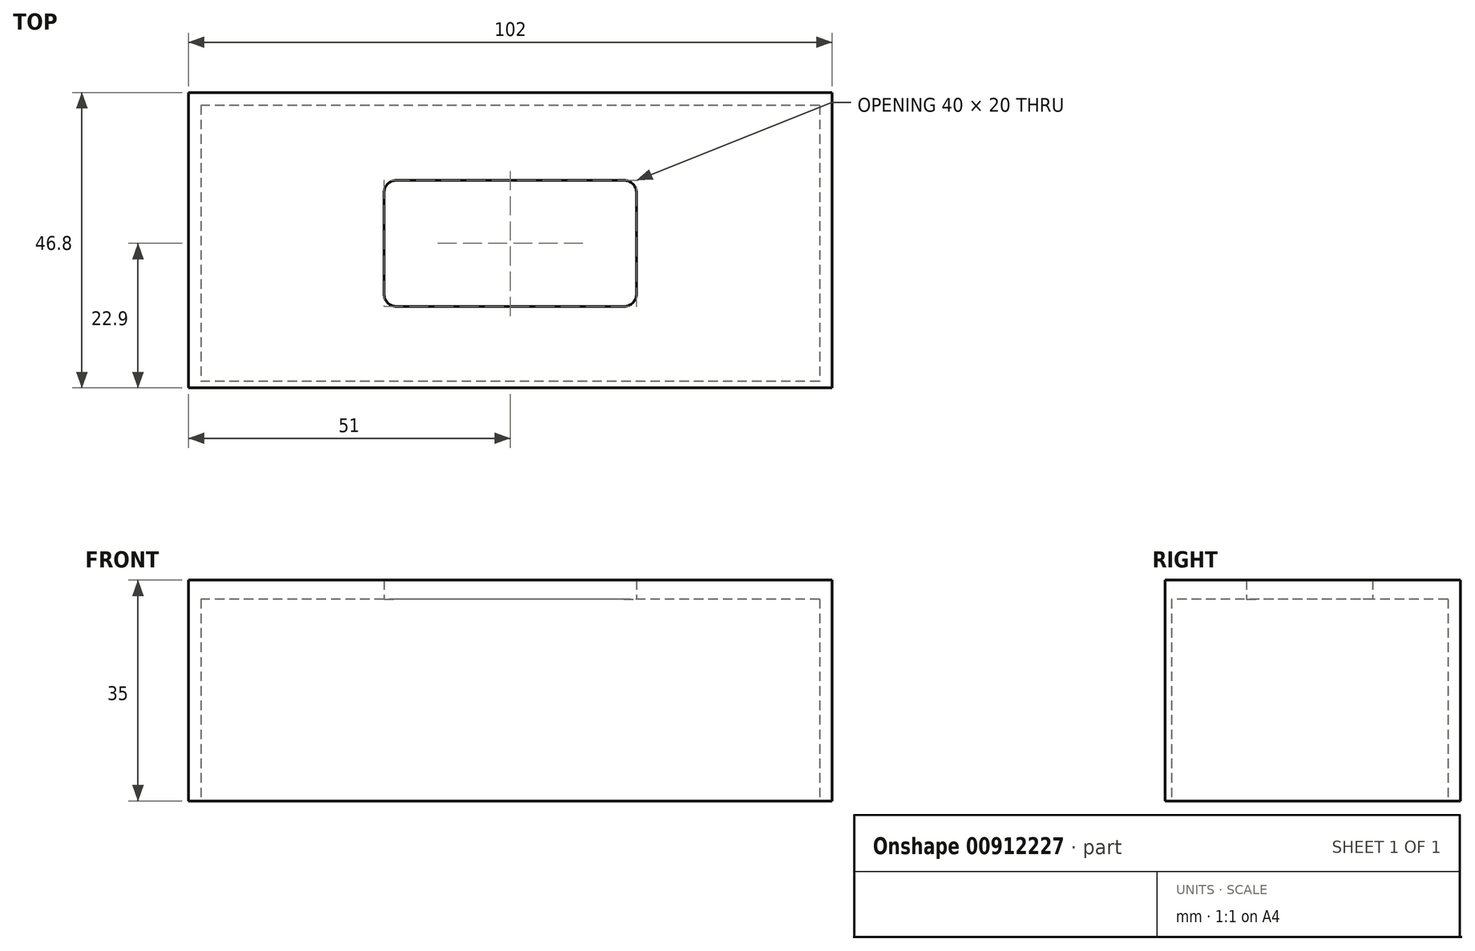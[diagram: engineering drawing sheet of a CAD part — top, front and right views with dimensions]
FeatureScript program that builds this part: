
annotation { "Feature Type Name" : "Feature", "Feature Type Description" : "" }
export const myFeature = defineFeature(function(context is Context, id is Id, definition is map)
    precondition{}
    {
        {
            var Q0;
            Q0=qCreatedBy(makeId("Top.planeOp"),FACE);
            var sketch = newSketch(context, id + "F0", { "sketchPlane" : qUnion([Q0])});
            skLineSegment(sketch, "E0.bottom", {"start": v(49, 21.9) * mm, "end": v(-49, 21.9) * mm});
            skLineSegment(sketch, "E0.top", {"start": v(49, -21.9) * mm, "end": v(-49, -21.9) * mm});
            skLineSegment(sketch, "E0.left", {"start": v(49, 21.9) * mm, "end": v(49, -21.9) * mm});
            skLineSegment(sketch, "E0.right", {"start": v(-49, 21.9) * mm, "end": v(-49, -21.9) * mm});
            skPoint(sketch, "E0.middle", {"position": v(0, 0) * mm});
            skLineSegment(sketch, "E1.0", {"start": v(51, 23.9) * mm, "end": v(-51, 23.9) * mm});
            skLineSegment(sketch, "E1.1", {"start": v(51, 23.9) * mm, "end": v(51, -22.9) * mm});
            skLineSegment(sketch, "E1.2", {"start": v(51, -22.9) * mm, "end": v(-51, -22.9) * mm});
            skLineSegment(sketch, "E1.3", {"start": v(-51, 23.9) * mm, "end": v(-51, -22.9) * mm});
            skSolve(sketch);
        }
        {
            var Q0;
            Q0=makeQuery(id+"F0.imprint","IMPRINT",FACE,{"disambiguationData":[TD([[makeQuery(id+"F0.imprint","IMPRINT",EDGE,{"derivedFrom":sQuery(id+"F0.wireOp",EDGE,"E0.bottom")}),-1.0]])]});
            extrude(context, id + "F1", {"entities" : qUnion([Q0]), "depth" : 32 * mm, "offsetDistance" : 25 * mm});
        }
        {
            var Q0;
            Q0=makeQuery(id+"F1.opExtrude","CAP_FACE",FACE,{"disambiguationData":[OSD([sQuery(id+"F0.wireOp",EDGE,"E0.bottom"),sQuery(id+"F0.wireOp",EDGE,"E0.top"),sQuery(id+"F0.wireOp",EDGE,"E0.left"),sQuery(id+"F0.wireOp",EDGE,"E0.right"),sQuery(id+"F0.wireOp",EDGE,"E1.0"),sQuery(id+"F0.wireOp",EDGE,"E1.1"),sQuery(id+"F0.wireOp",EDGE,"E1.2"),sQuery(id+"F0.wireOp",EDGE,"E1.3")])],"isStart":false});
            var sketch = newSketch(context, id + "F2", { "sketchPlane" : qUnion([Q0])});
            skLineSegment(sketch, "E2.bottom", {"start": v(-51, 23.9) * mm, "end": v(51, 23.9) * mm});
            skLineSegment(sketch, "E2.top", {"start": v(-51, -22.9) * mm, "end": v(51, -22.9) * mm});
            skLineSegment(sketch, "E2.left", {"start": v(-51, 23.9) * mm, "end": v(-51, -22.9) * mm});
            skLineSegment(sketch, "E2.right", {"start": v(51, 23.9) * mm, "end": v(51, -22.9) * mm});
            skLineSegment(sketch, "E3.bottom", {"start": v(18, 10) * mm, "end": v(-18, 10) * mm});
            skLineSegment(sketch, "E3.top", {"start": v(18, -10) * mm, "end": v(-18, -10) * mm});
            skLineSegment(sketch, "E3.left", {"start": v(20, 8) * mm, "end": v(20, -8) * mm});
            skLineSegment(sketch, "E3.right", {"start": v(-20, 8) * mm, "end": v(-20, -8) * mm});
            skPoint(sketch, "E3.middle", {"position": v(0, 0) * mm});
            skPoint(sketch, "E4.visualSharp", {"position": v(20, 10) * mm});
            skArc(sketch, "E4.filletArc", {"start": v(20, 8) * mm, "mid": v(19.41, 9.41) * mm, "end": v(18, 10) * mm});
            skPoint(sketch, "E5.visualSharp", {"position": v(20, -10) * mm});
            skArc(sketch, "E5.filletArc", {"start": v(18, -10) * mm, "mid": v(19.41, -9.41) * mm, "end": v(20, -8) * mm});
            skPoint(sketch, "E6.visualSharp", {"position": v(-20, -10) * mm});
            skArc(sketch, "E6.filletArc", {"start": v(-20, -8) * mm, "mid": v(-19.41, -9.41) * mm, "end": v(-18, -10) * mm});
            skPoint(sketch, "E7.visualSharp", {"position": v(-20, 10) * mm});
            skArc(sketch, "E7.filletArc", {"start": v(-18, 10) * mm, "mid": v(-19.41, 9.41) * mm, "end": v(-20, 8) * mm});
            skSolve(sketch);
        }
        {
            var Q0;
            Q0=makeQuery(id+"F2.imprint","IMPRINT",FACE,{"disambiguationData":[TD([[makeQuery(id+"F2.imprint","IMPRINT",EDGE,{"derivedFrom":sQuery(id+"F2.wireOp",EDGE,"E3.bottom")}),-1.0]])]});
            var Q1;
            Q1=makeQuery(id+"F2.imprint","IMPRINT",FACE,{"disambiguationData":[TD([[makeQuery(id+"F2.imprint","IMPRINT",EDGE,{"derivedFrom":sQuery(id+"F2.wireOp",EDGE,"E2.bottom")}),1.0]])]});
            extrude(context, id + "F3", {"entities" : qUnion([Q0, Q1]), "operationType" : NewBodyOperationType.ADD, "depth" : 3 * mm, "offsetDistance" : 25 * mm});
        }
    });
